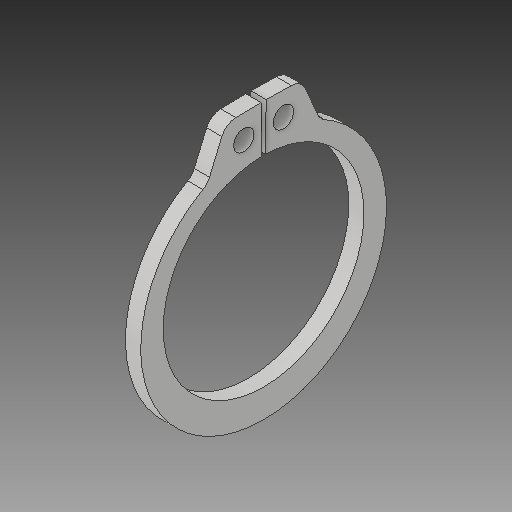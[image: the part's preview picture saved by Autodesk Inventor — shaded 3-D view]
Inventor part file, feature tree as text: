
AUTODESK INVENTOR PART (.ipt)
format: ipt  version: 2018 (Build 220112000, 112)  size: 114,176 bytes
history: native  units: in
note: dims shown in document units (in); Inventor stores cm internally (conversion verified against a paired STEP export)
features: fillet x1
ambient origin geometry x8: Origin, YZ Plane, XZ Plane, XY Plane, X Axis, Y Axis, Z Axis, Center Point
bodies: Solid1 (feature_tree)
feature tree (1):
  fillet  "Fillet1"  [1 undecoded]
note: 1 required parameter value undecoded (feature->parameter linkage not recoverable at this tier; creation-order binding heuristic only, values carry confidence <= 0.55)
